# Revit family: SonoMeter40_DN40_RFA
name_source: partatom
category: Pipe Accessories
revit_build: Autodesk Revit 2017 (Build: 20161205_1400(x64)
units: mm (PartAtom-declared; Revit-internal decimal feet)

## family parameters
Always vertical = Yes
Cut with Voids When Loaded = No
Part Type = Valve - Breaks Into
Round Connector Dimension = Use Diameter
Shared = No
Work Plane-Based = No

## types (1)
- SonoMeter40_DN40_G2_Kvs23.57_300mm
    A = 60.00°
    A_H = 79 mm
    A_H1 = 50 mm  [stored 0.164042 ft]
    Body Material = Danfoss Brass
    Connection = G2B
    D = 40 mm  [stored 0.131234 ft]
    D1 = 50 mm  [stored 0.164042 ft]
    D2 = 60 mm  [stored 0.19685 ft]
    D3 = 80 mm
    Description = Energy Meter
    H = 79 mm
    IfcExportAs = IfcValveType
    IfcExportType = SonoMeter40
    Kvs = 23.6 m³/h
    L = 300 mm  [stored 0.984252 ft]
    L1 = 437 mm
    L2 = 21 mm  [stored 0.0688976 ft]
    L3 = 84 mm  [stored 0.275591 ft]
    L4 = 20 mm  [stored 0.0656168 ft]
    L5 = 24 mm
    LOD 200 = No
    LOD 350 = Yes
    Manufacturer = Danfoss
    Max Flow = 20 m3/h
    Min Flow = 0.1 m3/h
    Model = SonoMeter40
    Model Type = SonoMeter40_DN40_G2_Kvs23.57_300mm
    Nominal Flow = 10 m3/h
    Operation Pressure = PN25
    URL = https://store.danfoss.com
    Weight = 3.70 kg

note: [stored X ft] marks values corroborated as IEEE doubles in the binary element streams (Revit-internal decimal feet)

## geometry (parser evidence)
native form markers: Sweep x9
no freeform markers — native parametric forms only
